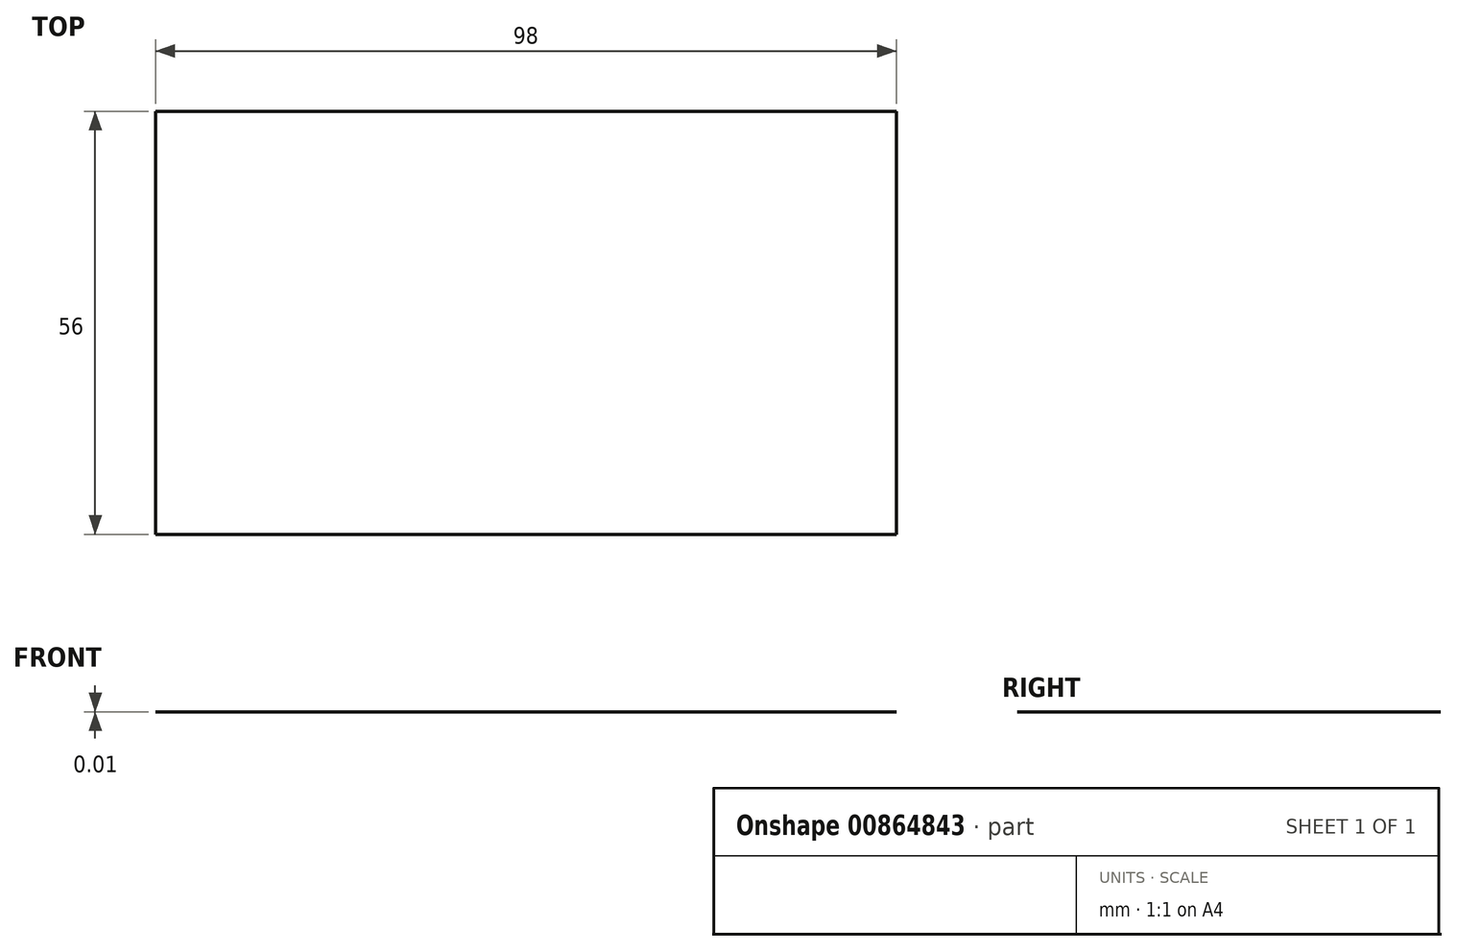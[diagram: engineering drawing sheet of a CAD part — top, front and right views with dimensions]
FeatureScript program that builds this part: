
annotation { "Feature Type Name" : "Feature", "Feature Type Description" : "" }
export const myFeature = defineFeature(function(context is Context, id is Id, definition is map)
    precondition{}
    {
        {
            var Q0;
            Q0=qCreatedBy(makeId("Top.planeOp"),FACE);
            var sketch = newSketch(context, id + "F0", { "sketchPlane" : qUnion([Q0])});
            skLineSegment(sketch, "E0.bottom", {"start": v(0, 0) * mm, "end": v(98, 0) * mm});
            skLineSegment(sketch, "E0.top", {"start": v(0, 56) * mm, "end": v(98, 56) * mm});
            skLineSegment(sketch, "E0.left", {"start": v(0, 0) * mm, "end": v(0, 56) * mm});
            skLineSegment(sketch, "E0.right", {"start": v(98, 0) * mm, "end": v(98, 56) * mm});
            skSolve(sketch);
        }
        {
            var Q0;
            Q0 = qSketchRegion(id + "F0", true);
            extrude(context, id + "F1", {"entities" : qUnion([Q0]), "depth" : 0.01 * mm, "offsetDistance" : 25 * mm});
        }
    });
